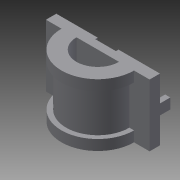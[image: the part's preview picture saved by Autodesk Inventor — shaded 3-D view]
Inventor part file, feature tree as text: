
AUTODESK INVENTOR PART (.ipt)
format: ipt  version: 2015 SP2 (Build 190223200, 223)  size: 145,408 bytes
history: native  units: in
note: dims shown in document units (in); Inventor stores cm internally (conversion verified against a paired STEP export)
features: other x5, extrude x4, sketch x1
ambient origin geometry x8: Origin, YZ Plane, XZ Plane, XY Plane, X Axis, Y Axis, Z Axis, Center Point
bodies: Solid1 (feature_tree)
feature tree (10):
  extrude  "base_extrusion"  Depth=1.2in
  other  "moon_revolution"
  extrude  "cutout_extrusion"  Depth=0.2in TaperAngle=0.0deg
  extrude  "peg_extrusion"  Depth=0.7in
  extrude  "Extrusion4"  Depth=0.2in
  other  "base_sketch"
  other  "moon_sketch"
  other  "cutout_sketch"
  other  "peg_sketch"
  sketch  "Sketch6"  dims[d0=2.0in d1=1.2in d2=0.2in d3=0.0in d4=0.7in d5=0.2in d6=0.09in d7=180.0deg d16=0.2in d17=0.2in d18=0.0in d19=0.2in d20=0.1in d21=0.2in d22=0.1in d23=0.2in d24=0.0in d25=0.4in d26=0.05in d27=0.2in d28=0.0in d9=1.0in d10=1.0in]
